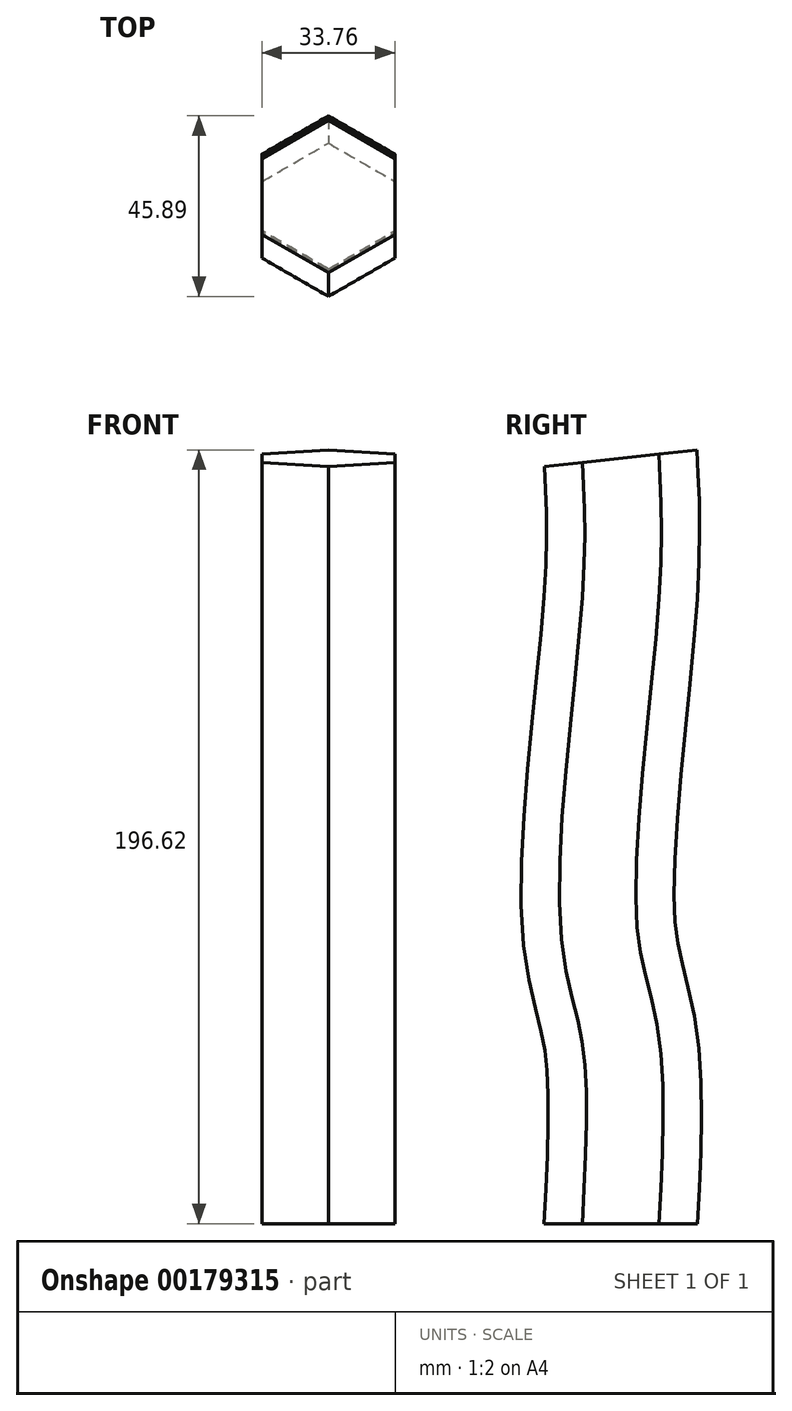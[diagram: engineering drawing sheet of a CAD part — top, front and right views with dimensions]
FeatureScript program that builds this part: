
annotation { "Feature Type Name" : "Feature", "Feature Type Description" : "" }
export const myFeature = defineFeature(function(context is Context, id is Id, definition is map)
    precondition{}
    {
        {
            var Q0;
            Q0=qCreatedBy(makeId("Top.planeOp"),FACE);
            var sketch = newSketch(context, id + "F0", { "sketchPlane" : qUnion([Q0])});
            skCircle(sketch, "E0.cCircle", {"center": v(0, 0) * mm, "radius": 16.88 * mm, "construction": true});
            skLineSegment(sketch, "E0.0", {"start": v(16.88, 9.74) * mm, "end": v(16.88, -9.74) * mm});
            skLineSegment(sketch, "E0.1", {"start": v(16.88, -9.74) * mm, "end": v(0, -19.49) * mm});
            skLineSegment(sketch, "E0.2", {"start": v(0, -19.49) * mm, "end": v(-16.88, -9.74) * mm});
            skLineSegment(sketch, "E0.3", {"start": v(-16.88, -9.74) * mm, "end": v(-16.88, 9.74) * mm});
            skLineSegment(sketch, "E0.4", {"start": v(-16.88, 9.74) * mm, "end": v(0, 19.49) * mm});
            skLineSegment(sketch, "E0.5", {"start": v(0, 19.49) * mm, "end": v(16.88, 9.74) * mm});
            skPoint(sketch, "E0.0.midPoint", {"position": v(16.88, 0) * mm});
            skSolve(sketch);
        }
        {
            var Q0;
            Q0=qCreatedBy(makeId("Right.planeOp"),FACE);
            var sketch = newSketch(context, id + "F1", { "sketchPlane" : qUnion([Q0])});
            skFitSpline(sketch, "E1", {"points": [v(0, 0) * mm, v(0, 46.82) * mm, v(-5.67, 76.77) * mm, v(0, 158.95) * mm, v(0, 194.5) * mm], "startDerivative": vector(11.22, 206.35) * mm, "endDerivative": vector(-7.44, 137.07) * mm});
            skSolve(sketch);
        }
        {
            var Q0;
            Q0=makeQuery(id+"F0.imprint","IMPRINT",FACE,{"disambiguationData":[TD([[makeQuery(id+"F0.imprint","IMPRINT",EDGE,{"derivedFrom":sQuery(id+"F0.wireOp",EDGE,"E0.0")}),-1.0]])]});
            var Q1;
            Q1=sQuery(id+"F1.wireOp",EDGE,"E1");
            sweep(context, id + "F2", {"profiles" : qUnion([Q0]), "path" : qUnion([Q1])});
        }
    });
